FCSTD DOCUMENT  (FreeCAD 0.15R4671 (Git))
Label: template150x150
License: All rights reserved
LicenseURL: http://en.wikipedia.org/wiki/All_rights_reserved
objects: Sketcher::SketchObject×1
note: 1 computed .brp shape members not serialized (recipe doc carries the construction recipe); baked Part::Feature solids carry a one-line shape summary decoded from their .brp

FEATURE [Sketcher::SketchObject] Sketch
  sketch-geometry (8):
    g0: GeomPoint [constr] X=-75 Y=-75 Z=0
    g1: GeomPoint [constr] X=75 Y=-75 Z=0
    g2: GeomPoint [constr] X=-75 Y=75 Z=0
    g3: GeomPoint [constr] X=75 Y=75 Z=0
    g4: LineSegment StartX=-75 StartY=-75 StartZ=0 EndX=-75 EndY=75 EndZ=0
    g5: LineSegment StartX=-75 StartY=75 StartZ=0 EndX=75 EndY=75 EndZ=0
    g6: LineSegment StartX=75 StartY=75 StartZ=0 EndX=75 EndY=-75 EndZ=0
    g7: LineSegment StartX=75 StartY=-75 StartZ=0 EndX=-75 EndY=-75 EndZ=0
  constraints (11):
    c: Coincident(g4,g0)
    c: Coincident(g4,g2)
    c: Vertical(g4)
    c: Coincident(g5,g2)
    c: Coincident(g5,g3)
    c: Horizontal(g5)
    c: Coincident(g6,g3)
    c: Coincident(g6,g1)
    c: Vertical(g6)
    c: Coincident(g7,g0)
    c: Horizontal(g7)
